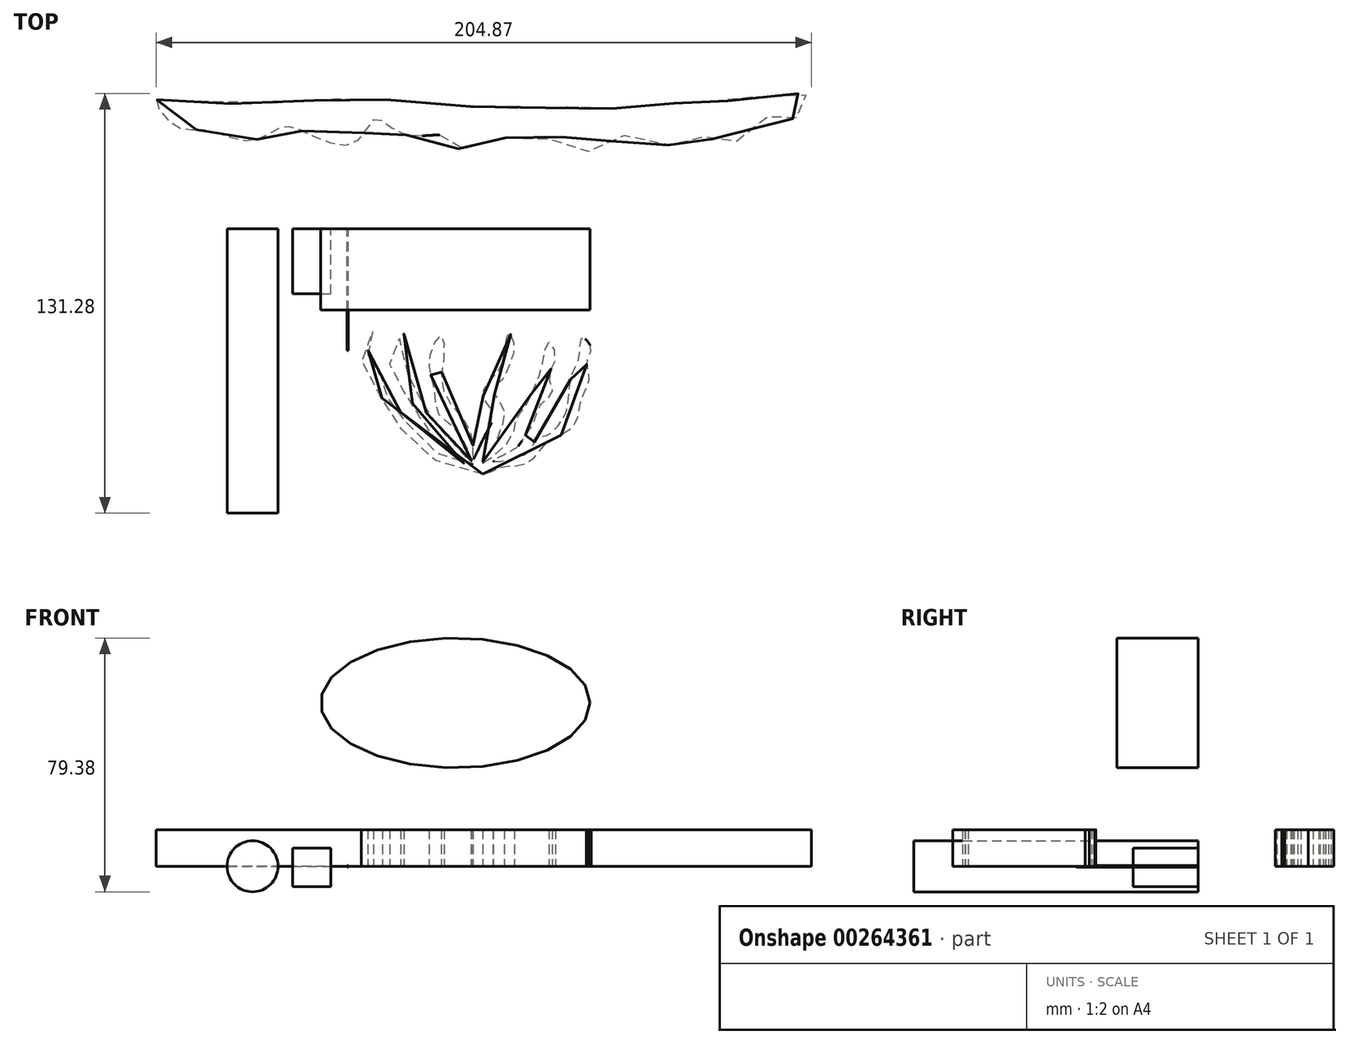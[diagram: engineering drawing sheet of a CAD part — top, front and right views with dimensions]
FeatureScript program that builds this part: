
annotation { "Feature Type Name" : "Feature", "Feature Type Description" : "" }
export const myFeature = defineFeature(function(context is Context, id is Id, definition is map)
    precondition{}
    {
        {
            var Q0;
            Q0=qCreatedBy(makeId("Front.planeOp"),FACE);
            var sketch = newSketch(context, id + "F0", { "sketchPlane" : qUnion([Q0])});
            skCircle(sketch, "E0", {"center": v(-72, 0) * mm, "radius": 7.97 * mm});
            skSolve(sketch);
        }
        {
            var Q0;
            Q0=makeQuery(id+"F0.imprint","IMPRINT",FACE,{"disambiguationData":[TD([[makeQuery(id+"F0.imprint","IMPRINT",EDGE,{"derivedFrom":sQuery(id+"F0.wireOp",EDGE,"E0")}),1.0]])]});
            extrude(context, id + "F1", {"entities" : qUnion([Q0]), "depth" : 88.9 * mm});
        }
        {
            var Q0;
            Q0=qCreatedBy(makeId("Front.planeOp"),FACE);
            var sketch = newSketch(context, id + "F2", { "sketchPlane" : qUnion([Q0])});
            skLineSegment(sketch, "E1.bottom", {"start": v(-59.52, -6.39) * mm, "end": v(-47.5, -6.39) * mm});
            skLineSegment(sketch, "E1.top", {"start": v(-59.52, 5.64) * mm, "end": v(-47.5, 5.64) * mm});
            skLineSegment(sketch, "E1.left", {"start": v(-59.52, -6.39) * mm, "end": v(-59.52, 5.64) * mm});
            skLineSegment(sketch, "E1.right", {"start": v(-47.5, -6.39) * mm, "end": v(-47.5, 5.64) * mm});
            skSolve(sketch);
        }
        {
            var Q0;
            Q0 = qSketchRegion(id + "F2", true);
            extrude(context, id + "F3", {"entities" : qUnion([Q0]), "depth" : 20.32 * mm});
        }
        {
            var Q0;
            Q0=qCreatedBy(makeId("Front.planeOp"),FACE);
            var sketch = newSketch(context, id + "F4", { "sketchPlane" : qUnion([Q0])});
            skCircle(sketch, "E2", {"center": v(-42.27, 0) * mm, "radius": 0.24 * mm});
            skSolve(sketch);
        }
        {
            var Q0;
            Q0 = qSketchRegion(id + "F4", true);
            extrude(context, id + "F5", {"entities" : qUnion([Q0]), "depth" : 38.1 * mm});
        }
        {
            var Q0;
            Q0=qCreatedBy(makeId("Top.planeOp"),FACE);
            var sketch = newSketch(context, id + "F6", { "sketchPlane" : qUnion([Q0])});
            skFitSpline(sketch, "E3", {"points": [v(-102.06, 40.4) * mm, v(-95.83, 32.1) * mm, v(-86.34, 30.9) * mm, v(-72.4, 27.64) * mm, v(-63.2, 31.8) * mm, v(-56.98, 30.9) * mm, v(-40.37, 26.75) * mm, v(-33.55, 34.46) * mm, v(-24.95, 29.72) * mm, v(-9.82, 28.53) * mm, v(-7.16, 24.68) * mm, v(0, 29.72) * mm, v(14.8, 26.16) * mm, v(24.28, 28.83) * mm, v(34.36, 24.08) * mm, v(42.96, 29.13) * mm, v(56.01, 26.16) * mm, v(64.32, 28.53) * mm, v(70.55, 28.53) * mm, v(77.07, 27.05) * mm, v(84.48, 30.9) * mm, v(90.71, 35.95) * mm, v(95.46, 34.46) * mm, v(101.98, 37.73) * mm, v(101.98, 41.29) * mm, v(87.15, 41.58) * mm, v(73.51, 39.8) * mm, v(64.32, 39.8) * mm, v(50.68, 38.02) * mm, v(37.63, 37.73) * mm, v(21.9, 38.02) * mm, v(4.7, 37.73) * mm, v(-20.5, 39.8) * mm, v(-41.26, 40.7) * mm, v(-58.76, 39.8) * mm, v(-86.04, 39.8) * mm, v(-102.06, 40.4) * mm]});
            skSolve(sketch);
        }
        {
            var Q0;
            Q0 = qSketchRegion(id + "F6", true);
            extrude(context, id + "F7", {"entities" : qUnion([Q0]), "depth" : 11.43 * mm});
        }
        {
            var Q0;
            Q0=qCreatedBy(makeId("Front.planeOp"),FACE);
            var sketch = newSketch(context, id + "F8", { "sketchPlane" : qUnion([Q0])});
            skEllipse(sketch, "E4", {"center": v(-8.64, 51.12) * mm, "majorRadius": 42.11 * mm, "minorRadius": 20.28 * mm, "majorAxis": v(1, 0)});
            skSolve(sketch);
        }
        {
            var Q0;
            Q0=makeQuery(id+"F8.imprint","IMPRINT",FACE,{"disambiguationData":[TD([[makeQuery(id+"F8.imprint","IMPRINT",EDGE,{"derivedFrom":sQuery(id+"F8.wireOp",EDGE,"E4")}),1.0]])]});
            extrude(context, id + "F9", {"entities" : qUnion([Q0]), "depth" : 25.4 * mm});
        }
        {
            var Q0;
            Q0=qCreatedBy(makeId("Top.planeOp"),FACE);
            var sketch = newSketch(context, id + "F10", { "sketchPlane" : qUnion([Q0])});
            skFitSpline(sketch, "E5", {"points": [v(0, -76.69) * mm, v(-19.35, -69.58) * mm, v(-28.15, -58.07) * mm, v(-35.26, -47.24) * mm, v(-37.63, -37.08) * mm, v(-34.25, -32) * mm, v(-35.94, -38.1) * mm, v(-34.59, -43.17) * mm, v(-31.54, -46.9) * mm, v(-31.2, -51.3) * mm, v(-27.14, -55.02) * mm, v(-24.43, -60.44) * mm, v(-20.7, -64.5) * mm, v(-15.97, -67.55) * mm, v(-14.95, -69.58) * mm, v(-3.78, -73.64) * mm, v(-11.56, -68.9) * mm, v(-18.34, -61.45) * mm, v(-21.72, -55.02) * mm, v(-26.46, -48.25) * mm, v(-29.17, -41.82) * mm, v(-27.48, -36.74) * mm, v(-24.77, -32.68) * mm, v(-25.44, -38.1) * mm, v(-25.1, -42.83) * mm, v(-20.7, -49.6) * mm, v(-17.66, -57.4) * mm, v(-13.26, -62.8) * mm, v(-10.55, -66.2) * mm, v(-5.47, -70.6) * mm, v(-3.44, -73.64) * mm, v(-7.16, -64.16) * mm, v(-13.93, -57.73) * mm, v(-14.95, -51.3) * mm, v(-16.64, -43.85) * mm, v(-15.63, -36.74) * mm, v(-12.92, -33.35) * mm, v(-12.24, -40.8) * mm, v(-12.92, -45.2) * mm, v(-11.56, -52.31) * mm, v(-6.49, -59.08) * mm, v(-3.78, -64.16) * mm, v(-3.1, -67.89) * mm, v(-3.1, -71.95) * mm, v(0, -65.86) * mm, v(3, -57.4) * mm, v(0, -51.97) * mm, v(2.65, -46.9) * mm, v(5.7, -42.83) * mm, v(7.06, -36.4) * mm, v(8.07, -32.34) * mm, v(9.76, -36.06) * mm, v(9.09, -40.46) * mm, v(7.06, -45.54) * mm, v(6.04, -47.24) * mm, v(3.33, -49.94) * mm, v(5.36, -54.34) * mm, v(6.72, -58.07) * mm, v(5.02, -64.16) * mm, v(3, -68.56) * mm, v(0, -72.96) * mm, v(8.75, -65.52) * mm, v(10.44, -59.42) * mm, v(13.15, -55.7) * mm, v(16.2, -49.27) * mm, v(18.57, -42.5) * mm, v(20.6, -35.39) * mm, v(22.63, -40.46) * mm, v(20.6, -45.88) * mm, v(21.61, -51.3) * mm, v(17.89, -55.02) * mm, v(16.2, -59.76) * mm, v(12.81, -65.18) * mm, v(9.76, -68.9) * mm, v(3.33, -72.63) * mm, v(14.5, -69.58) * mm, v(16.53, -65.52) * mm, v(20.26, -64.5) * mm, v(24.66, -59.76) * mm, v(26.35, -56.04) * mm, v(27.7, -45.88) * mm, v(30.08, -40.13) * mm, v(31.1, -34.03) * mm, v(33.8, -37.42) * mm, v(32.45, -41.14) * mm, v(33.12, -46.56) * mm, v(30.75, -53.33) * mm, v(29.74, -58.07) * mm, v(27.03, -62.8) * mm, v(19.58, -67.2) * mm, v(13.83, -73.3) * mm, v(5.36, -74.66) * mm, v(0, -76.69) * mm]});
            skSolve(sketch);
        }
        {
            var Q0;
            Q0 = qSketchRegion(id + "F10", true);
            extrude(context, id + "F11", {"entities" : qUnion([Q0]), "depth" : 11.43 * mm});
        }
    });
